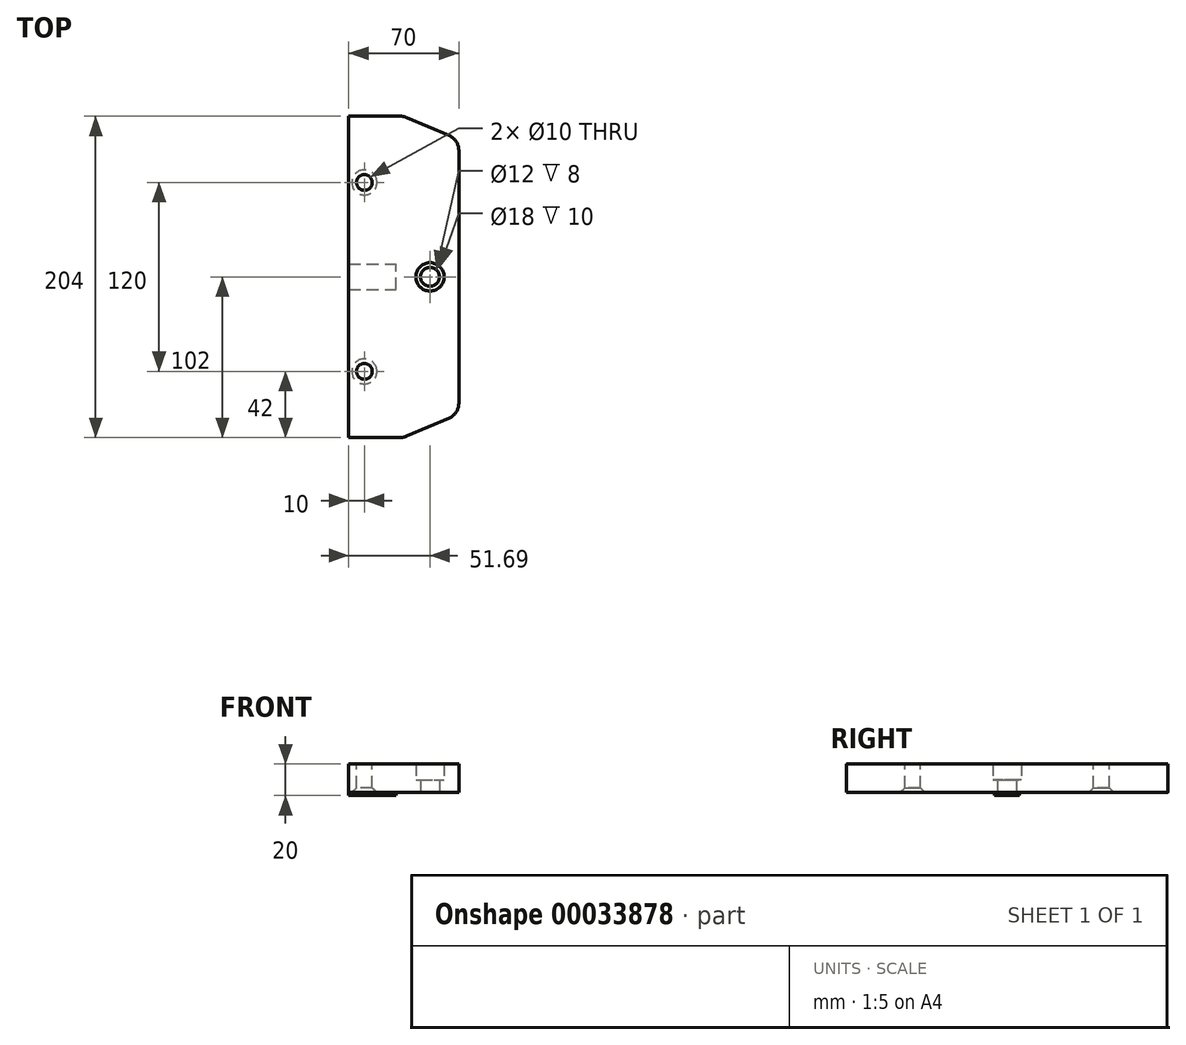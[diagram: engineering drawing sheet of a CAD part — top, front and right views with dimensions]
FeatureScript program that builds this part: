
annotation { "Feature Type Name" : "Feature", "Feature Type Description" : "" }
export const myFeature = defineFeature(function(context is Context, id is Id, definition is map)
    precondition{}
    {
        {
            var Q0;
            Q0=qCreatedBy(makeId("Top.planeOp"),FACE);
            var sketch = newSketch(context, id + "F0", { "sketchPlane" : qUnion([Q0])});
            skLineSegment(sketch, "E0.bottom", {"start": v(0, 0) * mm, "end": v(33, 0) * mm});
            skLineSegment(sketch, "E0.top", {"start": v(0, -204) * mm, "end": v(33, -204) * mm});
            skLineSegment(sketch, "E0.left", {"start": v(0, 0) * mm, "end": v(0, -204) * mm});
            skLineSegment(sketch, "E0.right", {"start": v(70, -21.59) * mm, "end": v(70, -182.41) * mm});
            skLineSegment(sketch, "E1", {"start": v(63.94, -191.6) * mm, "end": v(36.95, -203.19) * mm});
            skLineSegment(sketch, "E2", {"start": v(36.95, -0.81) * mm, "end": v(63.94, -12.4) * mm});
            skPoint(sketch, "E3.visualSharp", {"position": v(35.06, -204) * mm});
            skArc(sketch, "E3.filletArc", {"start": v(33, -204) * mm, "mid": v(35.01, -203.8) * mm, "end": v(36.95, -203.19) * mm});
            skPoint(sketch, "E4.visualSharp", {"position": v(70, -189) * mm});
            skArc(sketch, "E4.filletArc", {"start": v(63.94, -191.6) * mm, "mid": v(68.35, -187.91) * mm, "end": v(70, -182.41) * mm});
            skPoint(sketch, "E5.visualSharp", {"position": v(70, -15) * mm});
            skArc(sketch, "E5.filletArc", {"start": v(70, -21.59) * mm, "mid": v(68.35, -16.09) * mm, "end": v(63.94, -12.4) * mm});
            skPoint(sketch, "E6.visualSharp", {"position": v(35.06, 0) * mm});
            skArc(sketch, "E6.filletArc", {"start": v(36.95, -0.81) * mm, "mid": v(35.01, -0.2) * mm, "end": v(33, 0) * mm});
            skLineSegment(sketch, "E7", {"start": v(36.15, -102) * mm, "end": v(63.74, -102) * mm, "construction": true});
            skPoint(sketch, "E7.startSnap0", {"position": v(0, -102) * mm});
            skPoint(sketch, "E8", {"position": v(51.7, -102) * mm});
            skLineSegment(sketch, "E9", {"start": v(10, -162) * mm, "end": v(10, -42) * mm, "construction": true});
            skPoint(sketch, "E10", {"position": v(10, -102) * mm});
            skLineSegment(sketch, "E11.bottom", {"start": v(0, -110) * mm, "end": v(30, -110) * mm});
            skLineSegment(sketch, "E11.top", {"start": v(0, -94) * mm, "end": v(30, -94) * mm});
            skLineSegment(sketch, "E11.left", {"start": v(0, -110) * mm, "end": v(0, -94) * mm});
            skLineSegment(sketch, "E11.right", {"start": v(30, -110) * mm, "end": v(30, -94) * mm});
            skSolve(sketch);
        }
        {
            var Q0;
            Q0=makeQuery(id+"F0.imprint","IMPRINT",FACE,{"disambiguationData":[TD([[makeQuery(id+"F0.imprint","IMPRINT",EDGE,{"derivedFrom":sQuery(id+"F0.wireOp",EDGE,"E0.bottom")}),-1.0]])]});
            var Q1;
            Q1=makeQuery(id+"F0.imprint","IMPRINT",FACE,{"disambiguationData":[TD([[makeQuery(id+"F0.imprint","IMPRINT",EDGE,{"derivedFrom":sQuery(id+"F0.wireOp",EDGE,"E11.bottom")}),1.0]])]});
            extrude(context, id + "F1", {"entities" : qUnion([Q0, Q1]), "oppositeDirection" : true, "depth" : 18 * mm});
        }
        {
            var Q0;
            Q0=sQuery(id+"F0.wireOp",VERTEX,"E8");
            var Q1;
            Q1=makeQuery(id+"F1.opExtrude","SWEPT_BODY",BODY,{"disambiguationData":[OSD([sQuery(id+"F0.wireOp",EDGE,"E0.bottom"),sQuery(id+"F0.wireOp",EDGE,"E0.top"),sQuery(id+"F0.wireOp",EDGE,"E0.left"),sQuery(id+"F0.wireOp",EDGE,"E0.right"),sQuery(id+"F0.wireOp",EDGE,"E1"),sQuery(id+"F0.wireOp",EDGE,"E2"),sQuery(id+"F0.wireOp",EDGE,"E3.filletArc"),sQuery(id+"F0.wireOp",EDGE,"E4.filletArc"),sQuery(id+"F0.wireOp",EDGE,"E5.filletArc"),sQuery(id+"F0.wireOp",EDGE,"E6.filletArc")])]});
            hole(context, id + "F2", {"style" : HoleStyle.C_BORE, "holeDiameter" : 12 * mm, "cBoreDiameter" : 18 * mm, "cBoreDepth" : 10 * mm, "endStyle" : HoleEndStyle.THROUGH, "locations" : qUnion([Q0]), "scope" : qUnion([Q1])});
        }
        {
            var Q0;
            Q0=makeQuery(id+"F0.imprint","IMPRINT",FACE,{"disambiguationData":[TD([[makeQuery(id+"F0.imprint","IMPRINT",EDGE,{"derivedFrom":sQuery(id+"F0.wireOp",EDGE,"E11.bottom")}),1.0]])]});
            extrude(context, id + "F3", {"entities" : qUnion([Q0]), "operationType" : NewBodyOperationType.ADD, "oppositeDirection" : true, "depth" : 20 * mm});
        }
        {
            var Q0;
            Q0=makeQuery(id+"F1.opExtrude","CAP_FACE",FACE,{"disambiguationData":[OSD([sQuery(id+"F0.wireOp",EDGE,"E0.bottom"),sQuery(id+"F0.wireOp",EDGE,"E0.top"),sQuery(id+"F0.wireOp",EDGE,"E0.left"),sQuery(id+"F0.wireOp",EDGE,"E0.right"),sQuery(id+"F0.wireOp",EDGE,"E1"),sQuery(id+"F0.wireOp",EDGE,"E2"),sQuery(id+"F0.wireOp",EDGE,"E3.filletArc"),sQuery(id+"F0.wireOp",EDGE,"E4.filletArc"),sQuery(id+"F0.wireOp",EDGE,"E5.filletArc"),sQuery(id+"F0.wireOp",EDGE,"E6.filletArc"),sQuery(id+"F0.wireOp",EDGE,"E11.left")])],"isStart":false});
            var sketch = newSketch(context, id + "F5", { "sketchPlane" : qUnion([Q0])});
            skPoint(sketch, "E12", {"position": v(10, 42) * mm});
            skPoint(sketch, "E13", {"position": v(10, 162) * mm});
            skSolve(sketch);
        }
        {
            var Q0;
            Q0=sQuery(id+"F5.wireOp",VERTEX,"E13");
            var Q1;
            Q1=sQuery(id+"F5.wireOp",VERTEX,"E12");
            var Q2;
            Q2=makeQuery(id+"F1.opExtrude","SWEPT_BODY",BODY,{"disambiguationData":[OSD([sQuery(id+"F0.wireOp",EDGE,"E0.bottom"),sQuery(id+"F0.wireOp",EDGE,"E0.top"),sQuery(id+"F0.wireOp",EDGE,"E0.left"),sQuery(id+"F0.wireOp",EDGE,"E0.right"),sQuery(id+"F0.wireOp",EDGE,"E1"),sQuery(id+"F0.wireOp",EDGE,"E2"),sQuery(id+"F0.wireOp",EDGE,"E3.filletArc"),sQuery(id+"F0.wireOp",EDGE,"E4.filletArc"),sQuery(id+"F0.wireOp",EDGE,"E5.filletArc"),sQuery(id+"F0.wireOp",EDGE,"E6.filletArc"),sQuery(id+"F0.wireOp",EDGE,"E11.left")])]});
            hole(context, id + "F4", {"style" : HoleStyle.C_SINK, "holeDiameter" : 10 * mm, "cSinkDiameter" : 16 * mm, "endStyle" : HoleEndStyle.THROUGH, "locations" : qUnion([Q0, Q1]), "scope" : qUnion([Q2]), "cSinkAngle" : 90 * degree});
        }
    });
